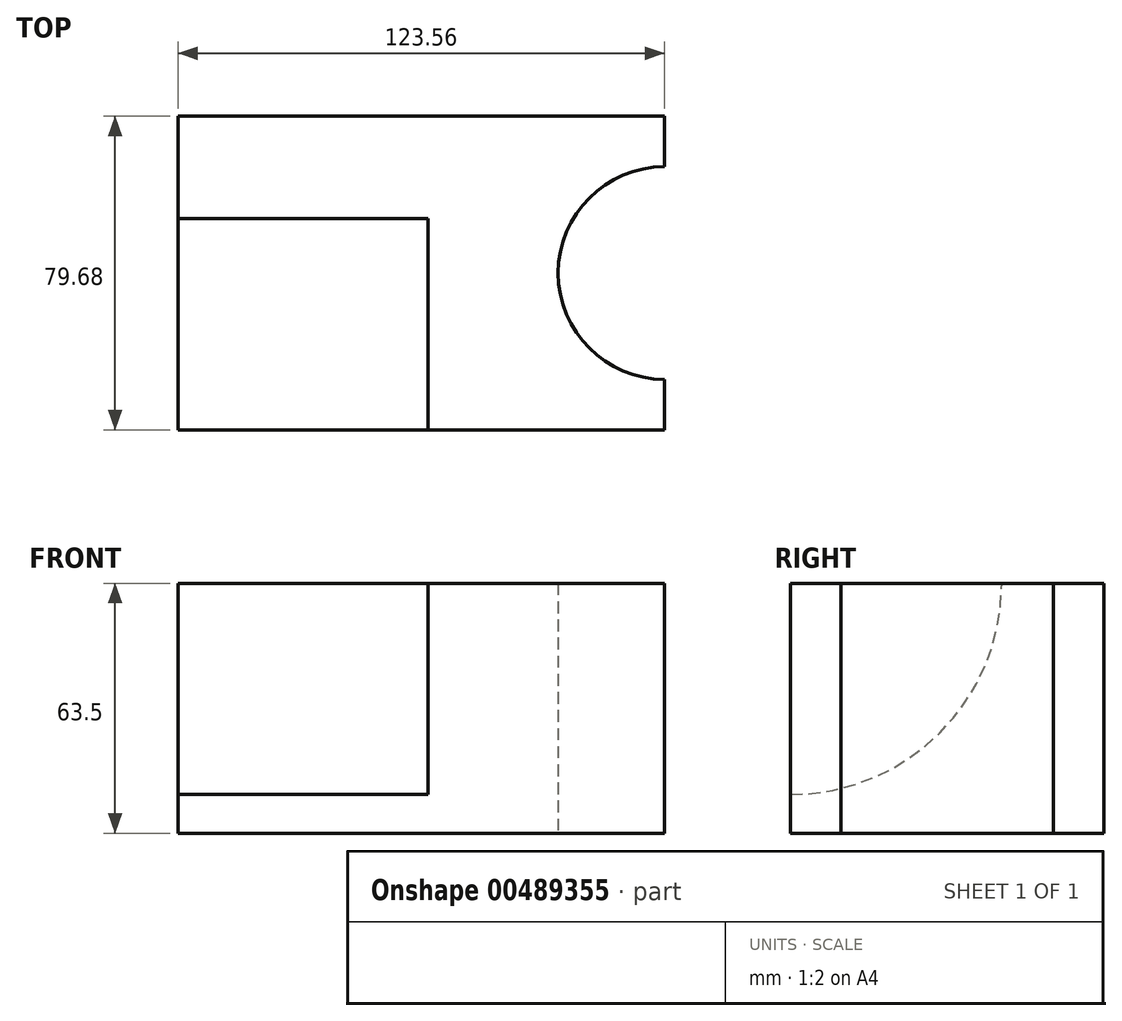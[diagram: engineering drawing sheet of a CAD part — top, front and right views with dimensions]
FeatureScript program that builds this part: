
annotation { "Feature Type Name" : "Feature", "Feature Type Description" : "" }
export const myFeature = defineFeature(function(context is Context, id is Id, definition is map)
    precondition{}
    {
        {
            var Q0;
            Q0=qCreatedBy(makeId("Top.planeOp"),FACE);
            var sketch = newSketch(context, id + "F0", { "sketchPlane" : qUnion([Q0])});
            skLineSegment(sketch, "E0.bottom", {"start": v(61.78, 39.84) * mm, "end": v(-61.78, 39.84) * mm});
            skLineSegment(sketch, "E0.top", {"start": v(61.78, -39.84) * mm, "end": v(-61.78, -39.84) * mm});
            skLineSegment(sketch, "E0.left", {"start": v(61.78, 39.84) * mm, "end": v(61.78, 27) * mm});
            skLineSegment(sketch, "E0.right", {"start": v(-61.78, 39.84) * mm, "end": v(-61.78, -39.84) * mm});
            skPoint(sketch, "E0.middle", {"position": v(0, 0) * mm});
            skArc(sketch, "E1", {"start": v(61.78, -27) * mm, "mid": v(34.77, 0) * mm, "end": v(61.78, 27) * mm});
            skLineSegment(sketch, "E2.trimOffspring", {"start": v(61.78, -27) * mm, "end": v(61.78, -39.84) * mm});
            skSolve(sketch);
        }
        {
            var Q0;
            Q0 = qSketchRegion(id + "F0", true);
            extrude(context, id + "F1", {"entities" : qUnion([Q0]), "depth" : 63.5 * mm});
        }
        {
            var Q0;
            Q0=makeQuery(id+"F1.opExtrude","SWEPT_FACE",FACE,{"disambiguationData":[OSD([sQuery(id+"F0.wireOp",EDGE,"E0.right")])]});
            var sketch = newSketch(context, id + "F2", { "sketchPlane" : qUnion([Q0])});
            skArc(sketch, "E3", {"start": v(-13.84, 63.5) * mm, "mid": v(1.88, 25.54) * mm, "end": v(39.84, 9.82) * mm});
            skLineSegment(sketch, "E4", {"start": v(39.84, 63.5) * mm, "end": v(39.84, 9.82) * mm});
            skLineSegment(sketch, "E5", {"start": v(39.84, 63.5) * mm, "end": v(-13.84, 63.5) * mm});
            skSolve(sketch);
        }
        {
            var Q0;
            Q0 = qSketchRegion(id + "F2", true);
            extrude(context, id + "F3", {"entities" : qUnion([Q0]), "operationType" : NewBodyOperationType.REMOVE, "oppositeDirection" : true, "depth" : 63.5 * mm});
        }
    });
